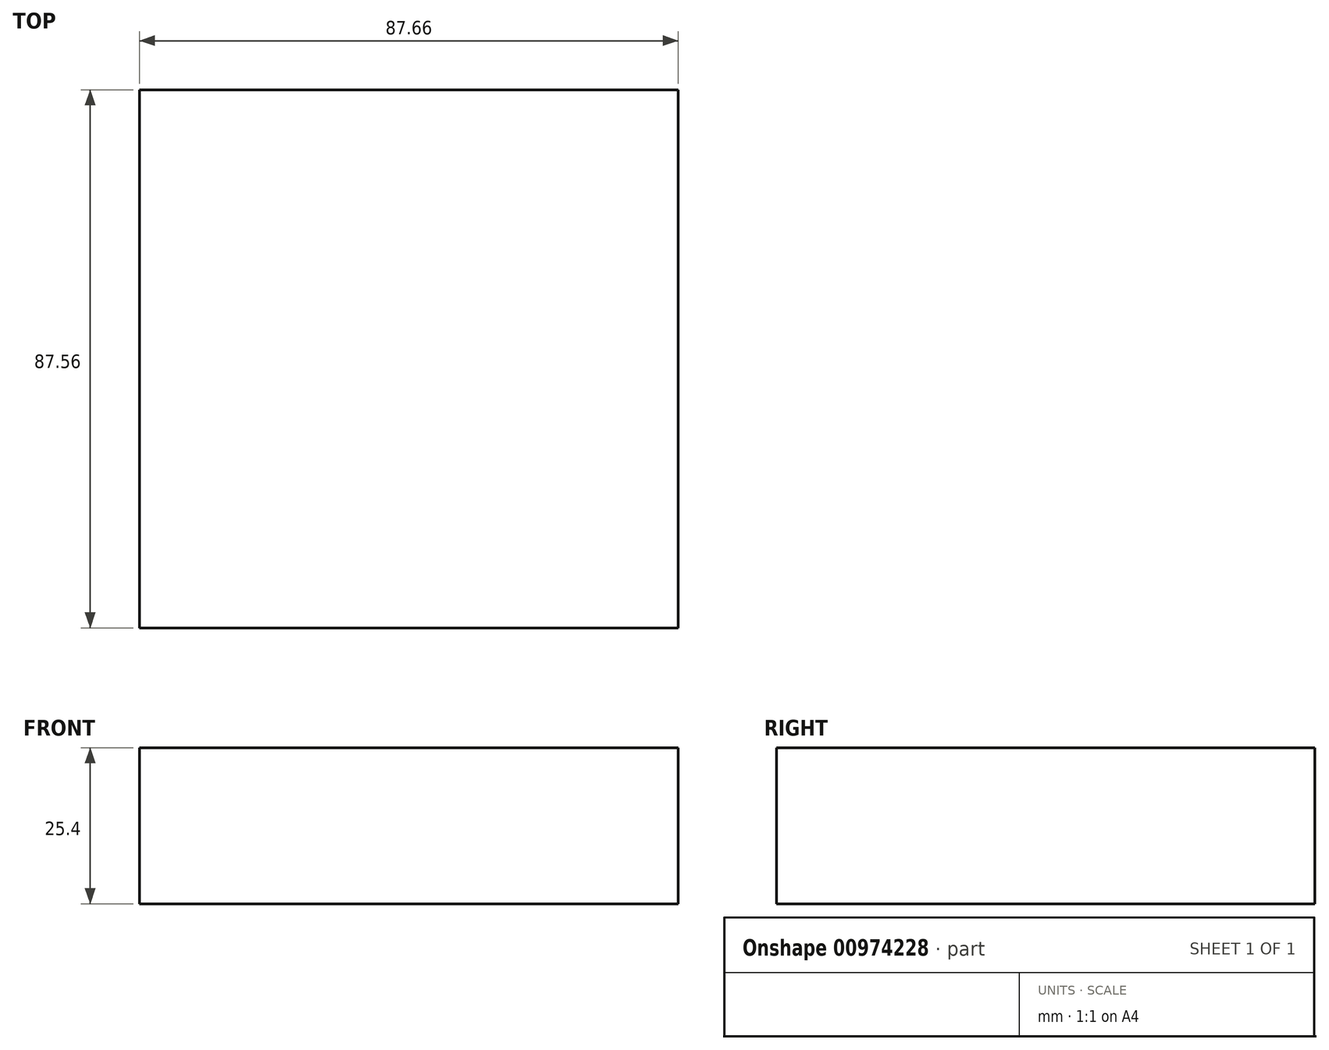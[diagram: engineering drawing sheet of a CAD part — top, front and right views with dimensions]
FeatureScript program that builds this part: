
annotation { "Feature Type Name" : "Feature", "Feature Type Description" : "" }
export const myFeature = defineFeature(function(context is Context, id is Id, definition is map)
    precondition{}
    {
        {
            var Q0;
            Q0=qCreatedBy(makeId("Top.planeOp"),FACE);
            var sketch = newSketch(context, id + "F0", { "sketchPlane" : qUnion([Q0])});
            skLineSegment(sketch, "E0.bottom", {"start": v(-44.32, -40.15) * mm, "end": v(43.34, -40.15) * mm});
            skLineSegment(sketch, "E0.top", {"start": v(-44.32, 47.41) * mm, "end": v(43.34, 47.41) * mm});
            skLineSegment(sketch, "E0.left", {"start": v(-44.32, -40.15) * mm, "end": v(-44.32, 47.41) * mm});
            skLineSegment(sketch, "E0.right", {"start": v(43.34, -40.15) * mm, "end": v(43.34, 47.41) * mm});
            skSolve(sketch);
        }
        {
            var Q0;
            Q0=makeQuery(id+"F0.imprint","IMPRINT",FACE,{"disambiguationData":[TD([[makeQuery(id+"F0.imprint","IMPRINT",EDGE,{"derivedFrom":sQuery(id+"F0.wireOp",EDGE,"E0.bottom")}),1.0]])]});
            extrude(context, id + "F1", {"entities" : qUnion([Q0]), "depth" : 25.4 * mm, "offsetDistance" : 25.4 * mm});
        }
    });
